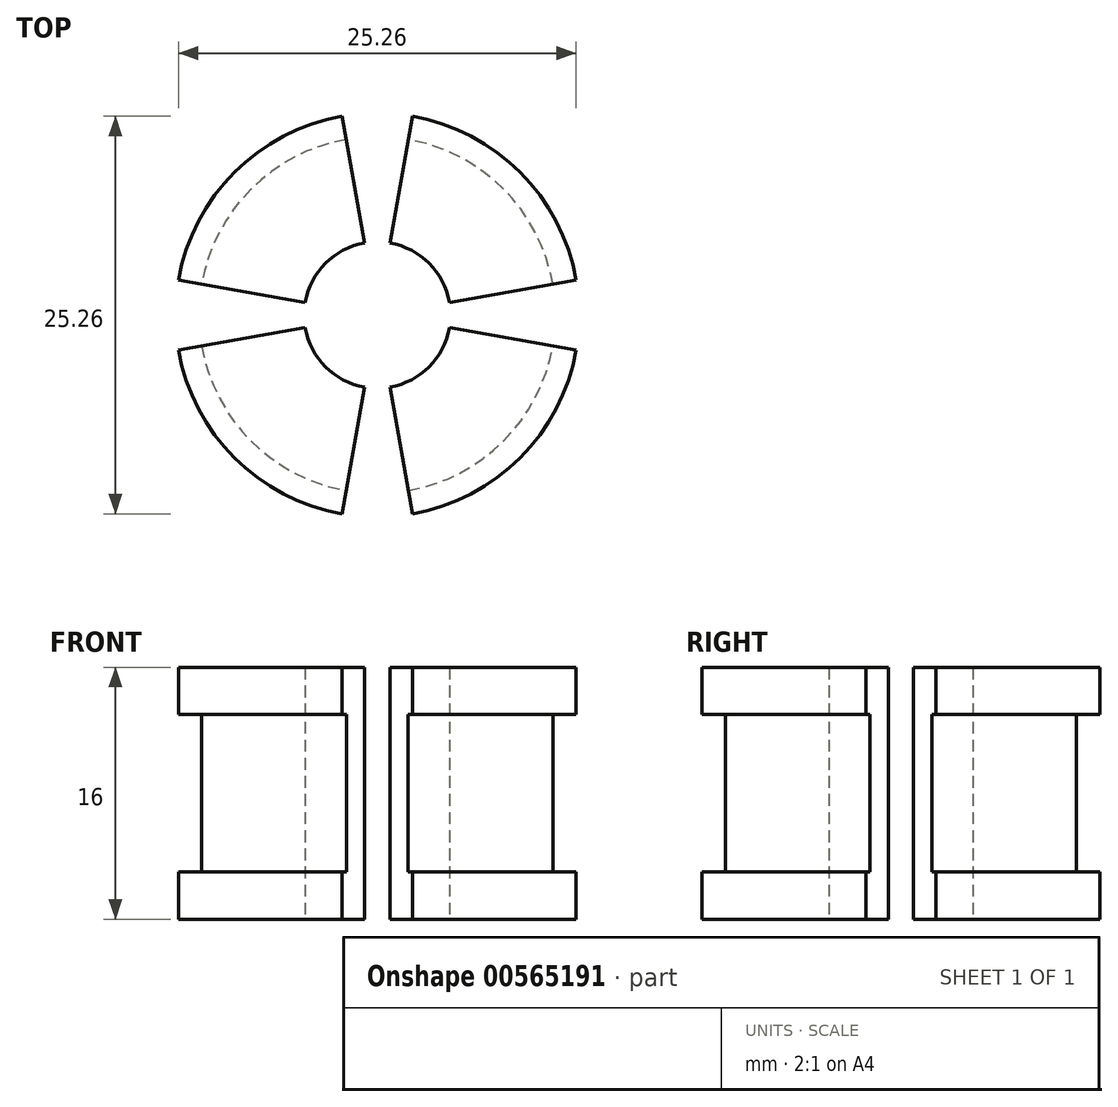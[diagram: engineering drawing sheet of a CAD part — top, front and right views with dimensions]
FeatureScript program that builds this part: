
annotation { "Feature Type Name" : "Feature", "Feature Type Description" : "" }
export const myFeature = defineFeature(function(context is Context, id is Id, definition is map)
    precondition{}
    {
        {
            var Q0;
            Q0=qCreatedBy(makeId("Front.planeOp"),FACE);
            var sketch = newSketch(context, id + "F0", { "sketchPlane" : qUnion([Q0])});
            skLineSegment(sketch, "E0", {"start": v(-4.65, 0) * mm, "end": v(-4.65, -16) * mm});
            skLineSegment(sketch, "E1", {"start": v(-12.83, -16) * mm, "end": v(-12.83, -13) * mm});
            skLineSegment(sketch, "E2", {"start": v(-12.82, -13) * mm, "end": v(-11.32, -13) * mm});
            skLineSegment(sketch, "E3", {"start": v(-11.32, -13) * mm, "end": v(-11.32, -3) * mm});
            skLineSegment(sketch, "E4", {"start": v(-11.32, -3) * mm, "end": v(-12.83, -3) * mm});
            skLineSegment(sketch, "E5", {"start": v(-12.83, -3) * mm, "end": v(-12.83, 0) * mm});
            skLineSegment(sketch, "E6", {"start": v(-12.83, 0) * mm, "end": v(-4.65, 0) * mm});
            skLineSegment(sketch, "E7", {"start": v(-12.83, -16) * mm, "end": v(-4.65, -16) * mm});
            skLineSegment(sketch, "E8", {"start": v(0, 4.72) * mm, "end": v(0, -22.61) * mm});
            skSolve(sketch);
        }
        {
            var Q0;
            Q0=makeQuery(id+"F0.imprint","IMPRINT",FACE,{"disambiguationData":[TD([[makeQuery(id+"F0.imprint","IMPRINT",EDGE,{"derivedFrom":sQuery(id+"F0.wireOp",EDGE,"E0")}),-1.0]])]});
            var Q1;
            Q1=sQuery(id+"F0.wireOp",EDGE,"E8");
            revolve(context, id + "F1", {"entities" : qUnion([Q0]), "axis" : qUnion([Q1]), "revolveType" : RevolveType.SYMMETRIC, "angle" : 70 * degree});
        }
        {
            var Q0;
            Q0=makeQuery(id+"F1.opRevolve","SWEPT_BODY",BODY,{"disambiguationData":[OSD([sQuery(id+"F0.wireOp",EDGE,"E0"),sQuery(id+"F0.wireOp",EDGE,"E1"),sQuery(id+"F0.wireOp",EDGE,"E2"),sQuery(id+"F0.wireOp",EDGE,"E3"),sQuery(id+"F0.wireOp",EDGE,"E4"),sQuery(id+"F0.wireOp",EDGE,"E5"),sQuery(id+"F0.wireOp",EDGE,"E6"),sQuery(id+"F0.wireOp",EDGE,"E7")])]});
            var Q1;
            Q1=makeQuery(id+"F1.opRevolve","SWEPT_FACE",FACE,{"disambiguationData":[OSD([sQuery(id+"F0.wireOp",EDGE,"E0")])]});
            circularPattern(context, id + "F2", {"entities" : qUnion([Q0]), "axis" : qUnion([Q1]), "angle" : 360 * degree, "instanceCount" : 4, "equalSpace" : true});
        }
        {
            var Q0;
            Q0=makeQuery(id+"F1.opRevolve","SWEPT_BODY",BODY,{"disambiguationData":[OSD([sQuery(id+"F0.wireOp",EDGE,"E0"),sQuery(id+"F0.wireOp",EDGE,"E1"),sQuery(id+"F0.wireOp",EDGE,"E2"),sQuery(id+"F0.wireOp",EDGE,"E3"),sQuery(id+"F0.wireOp",EDGE,"E4"),sQuery(id+"F0.wireOp",EDGE,"E5"),sQuery(id+"F0.wireOp",EDGE,"E6"),sQuery(id+"F0.wireOp",EDGE,"E7")])]});
            var Q1;
            Q1=makeQuery(id+"F2.opPattern","COPY",BODY,{"derivedFrom":makeQuery(id+"F1.opRevolve","SWEPT_BODY",BODY,{"disambiguationData":[OSD([sQuery(id+"F0.wireOp",EDGE,"E0"),sQuery(id+"F0.wireOp",EDGE,"E1"),sQuery(id+"F0.wireOp",EDGE,"E2"),sQuery(id+"F0.wireOp",EDGE,"E3"),sQuery(id+"F0.wireOp",EDGE,"E4"),sQuery(id+"F0.wireOp",EDGE,"E5"),sQuery(id+"F0.wireOp",EDGE,"E6"),sQuery(id+"F0.wireOp",EDGE,"E7")])]}),"instanceName":"2"});
            var Q2;
            Q2=makeQuery(id+"F2.opPattern","COPY",BODY,{"derivedFrom":makeQuery(id+"F1.opRevolve","SWEPT_BODY",BODY,{"disambiguationData":[OSD([sQuery(id+"F0.wireOp",EDGE,"E0"),sQuery(id+"F0.wireOp",EDGE,"E1"),sQuery(id+"F0.wireOp",EDGE,"E2"),sQuery(id+"F0.wireOp",EDGE,"E3"),sQuery(id+"F0.wireOp",EDGE,"E4"),sQuery(id+"F0.wireOp",EDGE,"E5"),sQuery(id+"F0.wireOp",EDGE,"E6"),sQuery(id+"F0.wireOp",EDGE,"E7")])]}),"instanceName":"1"});
            var Q3;
            Q3=makeQuery(id+"F2.opPattern","COPY",BODY,{"derivedFrom":makeQuery(id+"F1.opRevolve","SWEPT_BODY",BODY,{"disambiguationData":[OSD([sQuery(id+"F0.wireOp",EDGE,"E0"),sQuery(id+"F0.wireOp",EDGE,"E1"),sQuery(id+"F0.wireOp",EDGE,"E2"),sQuery(id+"F0.wireOp",EDGE,"E3"),sQuery(id+"F0.wireOp",EDGE,"E4"),sQuery(id+"F0.wireOp",EDGE,"E5"),sQuery(id+"F0.wireOp",EDGE,"E6"),sQuery(id+"F0.wireOp",EDGE,"E7")])]}),"instanceName":"3"});
            var Q4;
            Q4=makeQuery(id+"F1.opRevolve","SWEPT_FACE",FACE,{"disambiguationData":[OSD([sQuery(id+"F0.wireOp",EDGE,"E0")])]});
            transform(context, id + "F3", {"entities" : qUnion([Q0, Q1, Q2, Q3]), "transformType" : TransformType.ROTATION, "transformAxis" : qUnion([Q4]), "angle" : 45 * degree, "oppositeDirection" : true, "makeCopy" : false});
        }
    });
